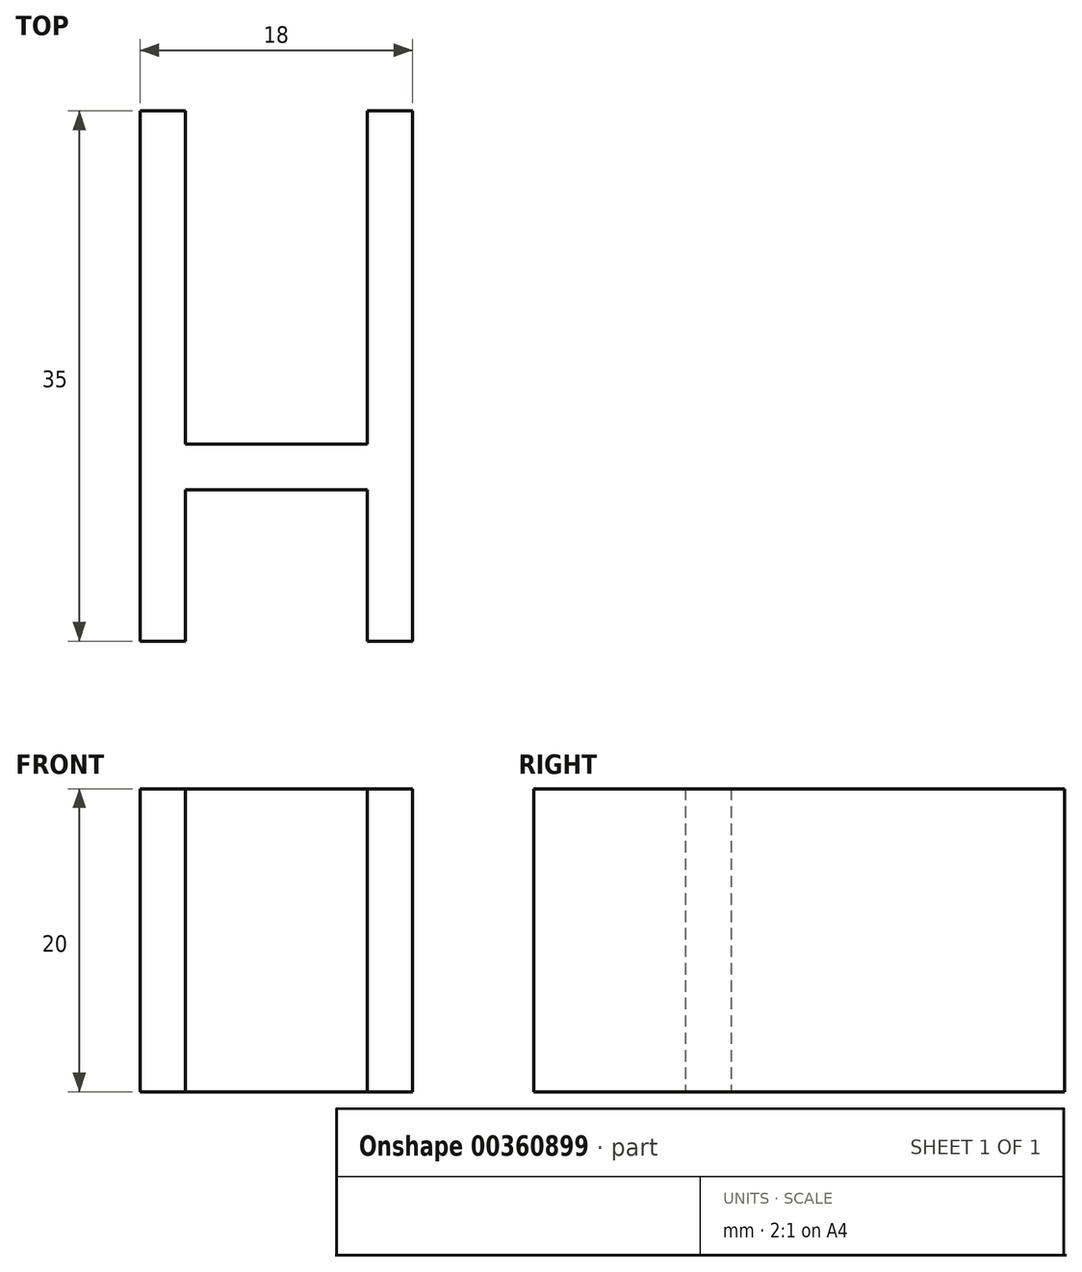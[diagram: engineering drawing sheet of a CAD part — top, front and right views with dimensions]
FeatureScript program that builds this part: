
annotation { "Feature Type Name" : "Feature", "Feature Type Description" : "" }
export const myFeature = defineFeature(function(context is Context, id is Id, definition is map)
    precondition{}
    {
        {
            var Q0;
            Q0=qCreatedBy(makeId("Top.planeOp"),FACE);
            var sketch = newSketch(context, id + "F0", { "sketchPlane" : qUnion([Q0])});
            skLineSegment(sketch, "E0", {"start": v(0, 0) * mm, "end": v(0, 22) * mm});
            skLineSegment(sketch, "E1", {"start": v(0, 22) * mm, "end": v(3, 22) * mm});
            skLineSegment(sketch, "E2", {"start": v(3, 22) * mm, "end": v(3, 0) * mm});
            skLineSegment(sketch, "E3", {"start": v(3, 0) * mm, "end": v(15, 0) * mm});
            skLineSegment(sketch, "E4", {"start": v(15, 0) * mm, "end": v(15, 22) * mm});
            skLineSegment(sketch, "E5", {"start": v(15, 22) * mm, "end": v(18, 22) * mm});
            skLineSegment(sketch, "E6", {"start": v(18, 22) * mm, "end": v(18, 0) * mm});
            skLineSegment(sketch, "E7", {"start": v(18, 0) * mm, "end": v(18, -13) * mm});
            skLineSegment(sketch, "E8", {"start": v(18, -13) * mm, "end": v(15, -13) * mm});
            skLineSegment(sketch, "E9", {"start": v(15, -13) * mm, "end": v(15, -3) * mm});
            skLineSegment(sketch, "E10", {"start": v(15, -3) * mm, "end": v(3, -3) * mm});
            skLineSegment(sketch, "E11", {"start": v(3, -3) * mm, "end": v(3, -13) * mm});
            skLineSegment(sketch, "E12", {"start": v(3, -13) * mm, "end": v(0, -13) * mm});
            skLineSegment(sketch, "E13", {"start": v(0, -13) * mm, "end": v(0, 0) * mm});
            skSolve(sketch);
        }
        {
            var Q0;
            Q0 = qSketchRegion(id + "F0", true);
            extrude(context, id + "F1", {"entities" : qUnion([Q0]), "depth" : 20 * mm});
        }
    });
